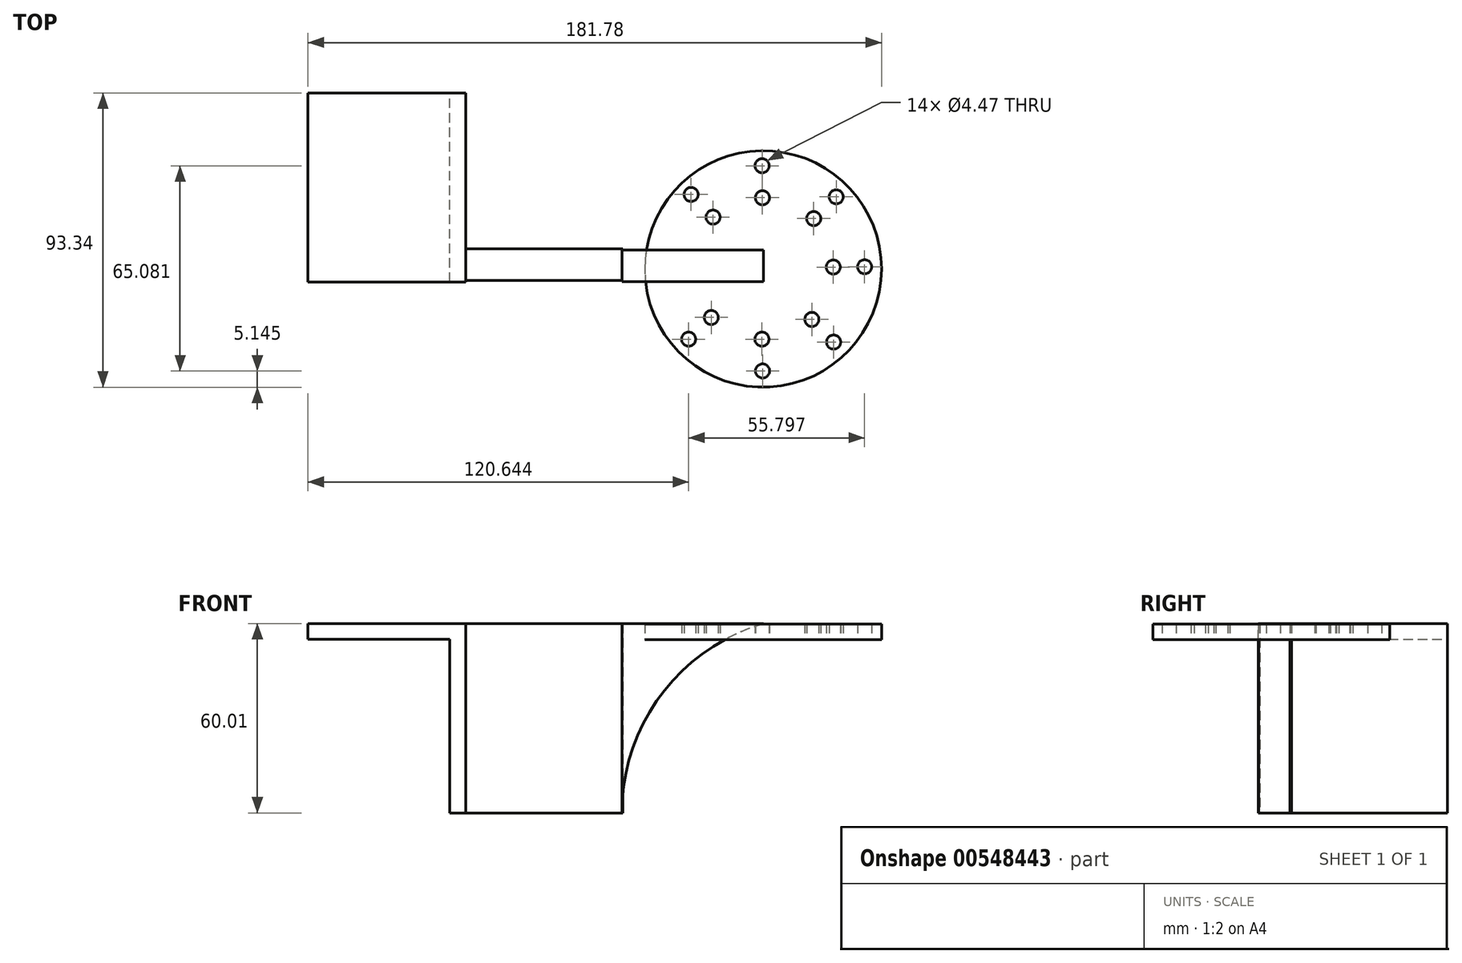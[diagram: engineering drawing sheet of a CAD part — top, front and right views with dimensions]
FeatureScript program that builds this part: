
annotation { "Feature Type Name" : "Feature", "Feature Type Description" : "" }
export const myFeature = defineFeature(function(context is Context, id is Id, definition is map)
    precondition{}
    {
        {
            var Q0;
            Q0=qCreatedBy(makeId("Front.planeOp"),FACE);
            var sketch = newSketch(context, id + "F0", { "sketchPlane" : qUnion([Q0])});
            skLineSegment(sketch, "E0", {"start": v(-62.57, 37.36) * mm, "end": v(-12.57, 37.36) * mm});
            skLineSegment(sketch, "E1", {"start": v(-12.57, 37.36) * mm, "end": v(-12.57, -22.64) * mm});
            skLineSegment(sketch, "E2", {"start": v(-12.57, -22.64) * mm, "end": v(-17.57, -22.64) * mm});
            skLineSegment(sketch, "E3", {"start": v(-17.57, -22.64) * mm, "end": v(-17.57, 32.36) * mm});
            skLineSegment(sketch, "E4", {"start": v(-17.57, 32.36) * mm, "end": v(-62.57, 32.36) * mm});
            skLineSegment(sketch, "E5", {"start": v(-62.57, 32.36) * mm, "end": v(-62.57, 37.36) * mm});
            skSolve(sketch);
        }
        {
            var Q0;
            Q0=makeQuery(id+"F0.imprint","IMPRINT",FACE,{"disambiguationData":[TD([[makeQuery(id+"F0.imprint","IMPRINT",EDGE,{"derivedFrom":sQuery(id+"F0.wireOp",EDGE,"E0")}),-1.0]])]});
            extrude(context, id + "F1", {"entities" : qUnion([Q0]), "depth" : 60 * mm, "offsetDistance" : 25 * mm});
        }
        {
            var Q0;
            Q0=qCreatedBy(makeId("Front.planeOp"),FACE);
            var sketch = newSketch(context, id + "F2", { "sketchPlane" : qUnion([Q0])});
            skLineSegment(sketch, "E6", {"start": v(-12.57, 37.36) * mm, "end": v(32.3, 37.36) * mm});
            skLineSegment(sketch, "E7", {"start": v(-12.57, 37.36) * mm, "end": v(-12.57, -22.63) * mm});
            skArc(sketch, "E8", {"start": v(32.3, 37.36) * mm, "mid": v(-0.11, 14.83) * mm, "end": v(-12.57, -22.63) * mm});
            skSolve(sketch);
        }
        {
            var Q0;
            Q0 = qSketchRegion(id + "F2", true);
            extrude(context, id + "F3", {"entities" : qUnion([Q0]), "depth" : 10 * mm, "offsetDistance" : 25 * mm});
        }
        {
            var Q0;
            Q0=makeQuery(id+"F3.opExtrude","SWEPT_BODY",BODY,{"disambiguationData":[OSD([sQuery(id+"F2.wireOp",EDGE,"E6"),sQuery(id+"F2.wireOp",EDGE,"E7"),sQuery(id+"F2.wireOp",EDGE,"E8")])]});
            transform(context, id + "F4", {"entities" : qUnion([Q0]), "transformType" : TransformType.TRANSLATION_3D, "dx" : 0 * mm, "dy" : -25 * mm, "dz" : 0 * mm, "makeCopy" : false});
        }
        {
            var Q0;
            Q0=qCreatedBy(makeId("Top.planeOp"),FACE);
            var sketch = newSketch(context, id + "F5", { "sketchPlane" : qUnion([Q0])});
            skCircle(sketch, "E9", {"center": v(32.2, -30.94) * mm, "radius": 37.5 * mm});
            skSolve(sketch);
        }
        {
            var Q0;
            Q0=makeQuery(id+"F5.imprint","IMPRINT",FACE,{"disambiguationData":[TD([[makeQuery(id+"F5.imprint","IMPRINT",EDGE,{"derivedFrom":sQuery(id+"F5.wireOp",EDGE,"E9")}),1.0]])]});
            extrude(context, id + "F6", {"entities" : qUnion([Q0]), "operationType" : NewBodyOperationType.ADD, "depth" : 5 * mm, "offsetDistance" : 25 * mm});
        }
        {
            var Q0;
            Q0=makeQuery(id+"F6.opExtrude","SWEPT_BODY",BODY,{"disambiguationData":[OSD([sQuery(id+"F5.wireOp",EDGE,"E9")])]});
            transform(context, id + "F7", {"entities" : qUnion([Q0]), "transformType" : TransformType.TRANSLATION_3D, "dx" : 0 * mm, "dy" : 0 * mm, "dz" : 32.3 * mm, "makeCopy" : false});
        }
        {
            var Q0;
            Q0=qCreatedBy(makeId("Top.planeOp"),FACE);
            var sketch = newSketch(context, id + "F8", { "sketchPlane" : qUnion([Q0])});
            skCircle(sketch, "E10", {"center": v(9.36, -7.3) * mm, "radius": 2.5 * mm});
            skCircle(sketch, "E11", {"center": v(16.33, -14.52) * mm, "radius": 2.5 * mm});
            skCircle(sketch, "E12", {"center": v(31.99, -8.34) * mm, "radius": 2.5 * mm});
            skCircle(sketch, "E13", {"center": v(31.9, 1.79) * mm, "radius": 2.5 * mm});
            skCircle(sketch, "E14", {"center": v(48.22, -14.97) * mm, "radius": 2.5 * mm});
            skCircle(sketch, "E15", {"center": v(55.37, -8.06) * mm, "radius": 2.5 * mm});
            skCircle(sketch, "E16", {"center": v(64.37, -30.27) * mm, "radius": 2.5 * mm});
            skCircle(sketch, "E17", {"center": v(54.43, -30.35) * mm, "radius": 2.5 * mm});
            skCircle(sketch, "E18", {"center": v(47.65, -46.95) * mm, "radius": 2.5 * mm});
            skCircle(sketch, "E19", {"center": v(54.54, -54.14) * mm, "radius": 2.5 * mm});
            skCircle(sketch, "E20", {"center": v(31.81, -53.22) * mm, "radius": 2.5 * mm});
            skCircle(sketch, "E21", {"center": v(32.02, -63.3) * mm, "radius": 2.5 * mm});
            skCircle(sketch, "E22", {"center": v(15.77, -46.33) * mm, "radius": 2.5 * mm});
            skCircle(sketch, "E23", {"center": v(8.57, -53.22) * mm, "radius": 2.5 * mm});
            skSolve(sketch);
        }
        {
            var Q0;
            Q0=sQuery(id+"F8.wireOp",VERTEX,"E12.center");
            var Q1;
            Q1=sQuery(id+"F8.wireOp",VERTEX,"E10.center");
            var Q2;
            Q2=sQuery(id+"F8.wireOp",VERTEX,"E11.center");
            var Q3;
            Q3=sQuery(id+"F8.wireOp",VERTEX,"E13.center");
            var Q4;
            Q4=sQuery(id+"F8.wireOp",VERTEX,"E14.center");
            var Q5;
            Q5=sQuery(id+"F8.wireOp",VERTEX,"E15.center");
            var Q6;
            Q6=sQuery(id+"F8.wireOp",VERTEX,"E17.center");
            var Q7;
            Q7=sQuery(id+"F8.wireOp",VERTEX,"E16.center");
            var Q8;
            Q8=sQuery(id+"F8.wireOp",VERTEX,"E18.center");
            var Q9;
            Q9=sQuery(id+"F8.wireOp",VERTEX,"E19.center");
            var Q10;
            Q10=sQuery(id+"F8.wireOp",VERTEX,"E21.center");
            var Q11;
            Q11=sQuery(id+"F8.wireOp",VERTEX,"E20.center");
            var Q12;
            Q12=sQuery(id+"F8.wireOp",VERTEX,"E22.center");
            var Q13;
            Q13=sQuery(id+"F8.wireOp",VERTEX,"E23.center");
            var Q14;
            Q14=sQuery(id+"F8.wireOp",VERTEX,"E22.center");
            var Q15;
            Q15=makeQuery(id+"F6.opExtrude","SWEPT_BODY",BODY,{"disambiguationData":[OSD([sQuery(id+"F5.wireOp",EDGE,"E9")])]});
            hole(context, id + "F9", {"style" : HoleStyle.SIMPLE, "endStyle" : HoleEndStyle.THROUGH, "oppositeDirection" : true, "holeDiameter" : 4.47 * mm, "isTappedThrough" : true, "tappedDepth" : 12 * mm, "tapClearance" : 3, "locations" : qUnion([Q0, Q1, Q2, Q3, Q4, Q5, Q6, Q7, Q8, Q9, Q10, Q11, Q12, Q13, Q14]), "scope" : qUnion([Q15])});
        }
        {
            var Q0;
            Q0=makeQuery(id+"F6.opExtrude","SWEPT_BODY",BODY,{"disambiguationData":[OSD([sQuery(id+"F5.wireOp",EDGE,"E9")])]});
            var Q1;
            Q1=makeQuery(id+"F3.opExtrude","SWEPT_BODY",BODY,{"disambiguationData":[OSD([sQuery(id+"F2.wireOp",EDGE,"E6"),sQuery(id+"F2.wireOp",EDGE,"E7"),sQuery(id+"F2.wireOp",EDGE,"E8")])]});
            transform(context, id + "F10", {"entities" : qUnion([Q0, Q1]), "transformType" : TransformType.TRANSLATION_3D, "dx" : 0 * mm, "dy" : -25.2 * mm, "dz" : 0 * mm, "makeCopy" : false});
        }
        {
            var Q0;
            Q0=makeQuery(id+"F6.opExtrude","SWEPT_BODY",BODY,{"disambiguationData":[OSD([sQuery(id+"F5.wireOp",EDGE,"E9")])]});
            var Q1;
            Q1=makeQuery(id+"F3.opExtrude","SWEPT_BODY",BODY,{"disambiguationData":[OSD([sQuery(id+"F2.wireOp",EDGE,"E6"),sQuery(id+"F2.wireOp",EDGE,"E7"),sQuery(id+"F2.wireOp",EDGE,"E8")])]});
            transform(context, id + "F11", {"entities" : qUnion([Q0, Q1]), "transformType" : TransformType.TRANSLATION_3D, "dx" : 0 * mm, "dy" : .3 * mm, "dz" : 0 * mm, "makeCopy" : false});
        }
        {
            var Q0;
            Q0=makeQuery(id+"F3.opExtrude","SWEPT_BODY",BODY,{"disambiguationData":[OSD([sQuery(id+"F2.wireOp",EDGE,"E6"),sQuery(id+"F2.wireOp",EDGE,"E7"),sQuery(id+"F2.wireOp",EDGE,"E8")])]});
            var Q1;
            Q1=makeQuery(id+"F6.opExtrude","SWEPT_BODY",BODY,{"disambiguationData":[OSD([sQuery(id+"F5.wireOp",EDGE,"E9")])]});
            transform(context, id + "F12", {"entities" : qUnion([Q0, Q1]), "transformType" : TransformType.TRANSLATION_3D, "dx" : 49.5 * mm, "dy" : 0 * mm, "dz" : 0 * mm, "makeCopy" : false});
        }
        {
            var Q0;
            Q0=qCreatedBy(makeId("Top.planeOp"),FACE);
            var sketch = newSketch(context, id + "F13", { "sketchPlane" : qUnion([Q0])});
            skLineSegment(sketch, "E24.bottom", {"start": v(37.26, -59.95) * mm, "end": v(-12.74, -59.95) * mm});
            skLineSegment(sketch, "E24.top", {"start": v(37.26, -49.95) * mm, "end": v(-12.74, -49.95) * mm});
            skLineSegment(sketch, "E24.left", {"start": v(37.26, -59.95) * mm, "end": v(37.26, -49.95) * mm});
            skLineSegment(sketch, "E24.right", {"start": v(-12.74, -59.95) * mm, "end": v(-12.74, -49.95) * mm});
            skSolve(sketch);
        }
        {
            var Q0;
            Q0 = qSketchRegion(id + "F13", true);
            extrude(context, id + "F14", {"entities" : qUnion([Q0]), "depth" : 60 * mm, "offsetDistance" : 25 * mm});
        }
        {
            var Q0;
            Q0=makeQuery(id+"F14.opExtrude","SWEPT_BODY",BODY,{"disambiguationData":[OSD([sQuery(id+"F13.wireOp",EDGE,"E24.bottom"),sQuery(id+"F13.wireOp",EDGE,"E24.top"),sQuery(id+"F13.wireOp",EDGE,"E24.left"),sQuery(id+"F13.wireOp",EDGE,"E24.right")])]});
            transform(context, id + "F15", {"entities" : qUnion([Q0]), "transformType" : TransformType.TRANSLATION_3D, "dx" : 0 * mm, "dy" : 0 * mm, "dz" : -22.7 * mm, "makeCopy" : false});
        }
        {
            var Q0;
            Q0=makeQuery(id+"F14.opExtrude","SWEPT_BODY",BODY,{"disambiguationData":[OSD([sQuery(id+"F13.wireOp",EDGE,"E24.bottom"),sQuery(id+"F13.wireOp",EDGE,"E24.top"),sQuery(id+"F13.wireOp",EDGE,"E24.left"),sQuery(id+"F13.wireOp",EDGE,"E24.right")])]});
            transform(context, id + "F16", {"entities" : qUnion([Q0]), "transformType" : TransformType.TRANSLATION_3D, "dx" : 0 * mm, "dy" : .5 * mm, "dz" : 0 * mm, "makeCopy" : false});
        }
        {
            var Q0;
            Q0=makeQuery(id+"F14.opExtrude","SWEPT_BODY",BODY,{"disambiguationData":[OSD([sQuery(id+"F13.wireOp",EDGE,"E24.bottom"),sQuery(id+"F13.wireOp",EDGE,"E24.top"),sQuery(id+"F13.wireOp",EDGE,"E24.left"),sQuery(id+"F13.wireOp",EDGE,"E24.right")])]});
            transform(context, id + "F17", {"entities" : qUnion([Q0]), "transformType" : TransformType.TRANSLATION_3D, "dx" : 0 * mm, "dy" : 0 * mm, "dz" : 0.05 * mm, "makeCopy" : false});
        }
    });
